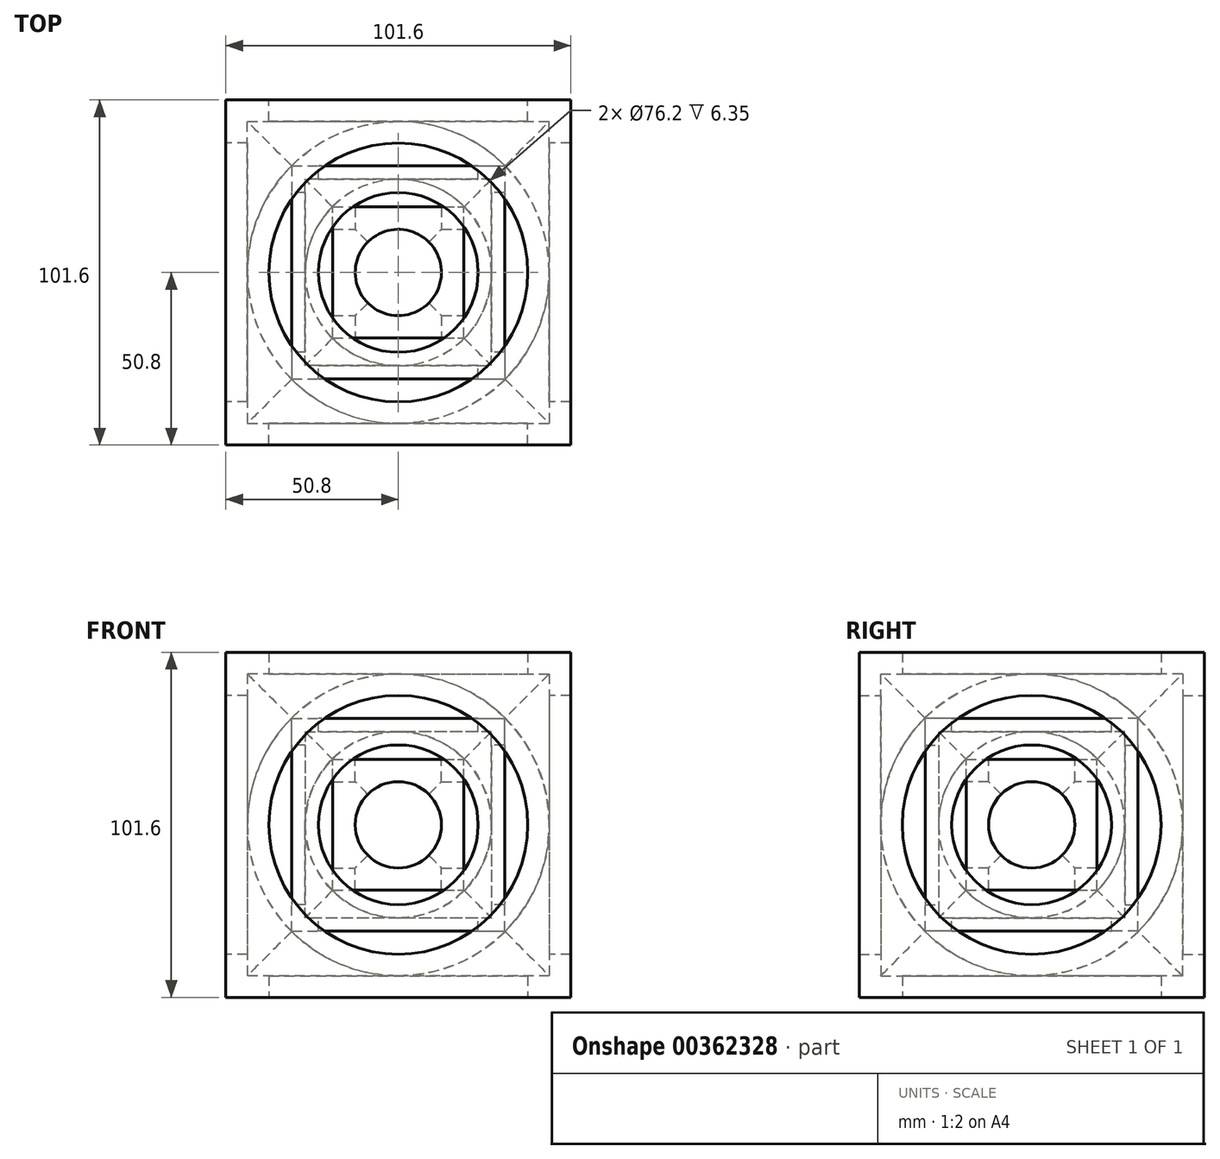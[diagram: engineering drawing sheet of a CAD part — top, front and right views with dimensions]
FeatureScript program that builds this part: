
annotation { "Feature Type Name" : "Feature", "Feature Type Description" : "" }
export const myFeature = defineFeature(function(context is Context, id is Id, definition is map)
    precondition{}
    {
        {
            var Q0;
            Q0=qCreatedBy(makeId("Front.planeOp"),FACE);
            var sketch = newSketch(context, id + "F0", { "sketchPlane" : qUnion([Q0])});
            skLineSegment(sketch, "E0.bottom", {"start": v(-50.8, 50.8) * mm, "end": v(50.8, 50.8) * mm});
            skLineSegment(sketch, "E0.top", {"start": v(-50.8, -50.8) * mm, "end": v(50.8, -50.8) * mm});
            skLineSegment(sketch, "E0.left", {"start": v(-50.8, 50.8) * mm, "end": v(-50.8, -50.8) * mm});
            skLineSegment(sketch, "E0.right", {"start": v(50.8, 50.8) * mm, "end": v(50.8, -50.8) * mm});
            skLineSegment(sketch, "E1", {"start": v(-50.8, 50.8) * mm, "end": v(50.8, -50.8) * mm, "construction": true});
            skSolve(sketch);
        }
        {
            var Q0;
            Q0 = qSketchRegion(id + "F0", true);
            extrude(context, id + "F1", {"entities" : qUnion([Q0]), "endBound" : BoundingType.SYMMETRIC, "depth" : 101.6 * mm});
        }
        {
            var Q0;
            Q0=qCreatedBy(makeId("Top.planeOp"),FACE);
            var sketch = newSketch(context, id + "F2", { "sketchPlane" : qUnion([Q0])});
            skLineSegment(sketch, "E2.bottom", {"start": v(-50.8, 0) * mm, "end": v(-31.34, 0) * mm});
            skLineSegment(sketch, "E2.top", {"start": v(-50.8, 38.1) * mm, "end": v(-44.45, 38.1) * mm});
            skLineSegment(sketch, "E2.left", {"start": v(-50.8, 0) * mm, "end": v(-50.8, 38.1) * mm});
            skLineSegment(sketch, "E3.left", {"start": v(-44.45, 38.1) * mm, "end": v(-44.45, 44.45) * mm});
            skLineSegment(sketch, "E4.bottom", {"start": v(0, 31.34) * mm, "end": v(0, 50.8) * mm});
            skLineSegment(sketch, "E4.top", {"start": v(-38.1, 44.45) * mm, "end": v(-38.1, 50.8) * mm});
            skLineSegment(sketch, "E4.left", {"start": v(0, 50.8) * mm, "end": v(-38.1, 50.8) * mm});
            skLineSegment(sketch, "E5.top", {"start": v(-44.45, 31.34) * mm, "end": v(-44.45, 44.45) * mm});
            skLineSegment(sketch, "E5.right", {"start": v(0, 31.34) * mm, "end": v(-44.45, 31.34) * mm});
            skLineSegment(sketch, "E6", {"start": v(-38.1, 44.45) * mm, "end": v(-44.45, 44.45) * mm});
            skLineSegment(sketch, "E7", {"start": v(-44.45, 44.45) * mm, "end": v(-31.34, 44.45) * mm});
            skLineSegment(sketch, "E8", {"start": v(-31.34, 44.45) * mm, "end": v(-31.34, 0) * mm});
            skLineSegment(sketch, "E9.bottom", {"start": v(-50.8, 50.8) * mm, "end": v(-38.1, 50.8) * mm, "construction": true});
            skLineSegment(sketch, "E9.top", {"start": v(-50.8, 38.1) * mm, "end": v(-38.1, 38.1) * mm, "construction": true});
            skLineSegment(sketch, "E9.left", {"start": v(-50.8, 50.8) * mm, "end": v(-50.8, 38.1) * mm, "construction": true});
            skLineSegment(sketch, "E9.right", {"start": v(-38.1, 50.8) * mm, "end": v(-38.1, 38.1) * mm, "construction": true});
            skLineSegment(sketch, "E10.MirrorCS", {"start": v(0, -31.34) * mm, "end": v(-44.45, -31.34) * mm});
            skLineSegment(sketch, "E11.MirrorCS", {"start": v(-44.45, -31.34) * mm, "end": v(-44.45, -44.45) * mm});
            skLineSegment(sketch, "E12.MirrorCS", {"start": v(0, -31.34) * mm, "end": v(0, -50.8) * mm});
            skLineSegment(sketch, "E13.MirrorCS", {"start": v(0, -50.8) * mm, "end": v(-38.1, -50.8) * mm});
            skLineSegment(sketch, "E14.MirrorCS", {"start": v(-38.1, -44.45) * mm, "end": v(-38.1, -50.8) * mm});
            skLineSegment(sketch, "E15.MirrorCS", {"start": v(-38.1, -44.45) * mm, "end": v(-44.45, -44.45) * mm});
            skLineSegment(sketch, "E16.MirrorCS", {"start": v(31.34, 44.45) * mm, "end": v(31.34, 0) * mm});
            skLineSegment(sketch, "E17.MirrorCS", {"start": v(44.45, 44.45) * mm, "end": v(31.34, 44.45) * mm});
            skLineSegment(sketch, "E18.MirrorCS", {"start": v(50.8, 0) * mm, "end": v(31.34, 0) * mm});
            skLineSegment(sketch, "E19.MirrorCS", {"start": v(50.8, 0) * mm, "end": v(50.8, 38.1) * mm});
            skLineSegment(sketch, "E20.MirrorCS", {"start": v(50.8, 38.1) * mm, "end": v(44.45, 38.1) * mm});
            skLineSegment(sketch, "E21.MirrorCS", {"start": v(44.45, 38.1) * mm, "end": v(44.45, 44.45) * mm});
            skSolve(sketch);
        }
        {
            var Q0;
            Q0=makeQuery(id+"F2.imprint","IMPRINT",FACE,{"disambiguationData":[TD([[makeQuery(id+"F2.imprint","IMPRINT",EDGE,{"derivedFrom":sQuery(id+"F2.wireOp",EDGE,"E2.bottom")}),1.0]])]});
            var Q1;
            {var subQ0=sQuery(id+"F2.wireOp",EDGE,"E5.top");Q1=makeQuery(id+"F2.imprint","IMPRINT",FACE,{"disambiguationData":[TD([[makeQuery(id+"F2.imprint","IMPRINT",EDGE,{"derivedFrom":subQ0}),-1.0]])]});}
            var Q2;
            Q2=makeQuery(id+"F2.imprint","IMPRINT",FACE,{"disambiguationData":[TD([[makeQuery(id+"F2.imprint","IMPRINT",EDGE,{"derivedFrom":sQuery(id+"F2.wireOp",EDGE,"E16.MirrorCS")}),1.0]])]});
            var Q3;
            Q3=sQuery(id+"F2.wireOp",EDGE,"E2.bottom");
            revolve(context, id + "F3", {"operationType" : NewBodyOperationType.REMOVE, "entities" : qUnion([Q0, Q1, Q2]), "axis" : qUnion([Q3]), "revolveType" : RevolveType.FULL});
        }
        {
            var Q0;
            Q0=makeQuery(id+"F2.imprint","IMPRINT",FACE,{"disambiguationData":[TD([[makeQuery(id+"F2.imprint","IMPRINT",EDGE,{"derivedFrom":sQuery(id+"F2.wireOp",EDGE,"E4.bottom")}),1.0]])]});
            var Q1;
            {var subQ0=sQuery(id+"F2.wireOp",EDGE,"E5.top");Q1=makeQuery(id+"F2.imprint","IMPRINT",FACE,{"disambiguationData":[TD([[makeQuery(id+"F2.imprint","IMPRINT",EDGE,{"derivedFrom":subQ0}),-1.0]])]});}
            var Q2;
            Q2=makeQuery(id+"F2.imprint","IMPRINT",FACE,{"disambiguationData":[TD([[makeQuery(id+"F2.imprint","IMPRINT",EDGE,{"derivedFrom":sQuery(id+"F2.wireOp",EDGE,"E10.MirrorCS")}),1.0]])]});
            var Q3;
            Q3=sQuery(id+"F2.wireOp",EDGE,"E4.bottom");
            revolve(context, id + "F4", {"operationType" : NewBodyOperationType.REMOVE, "entities" : qUnion([Q0, Q1, Q2]), "axis" : qUnion([Q3]), "revolveType" : RevolveType.FULL, "oppositeDirection" : true});
        }
        {
            var Q0;
            Q0=qCreatedBy(makeId("Front.planeOp"),FACE);
            var sketch = newSketch(context, id + "F5", { "sketchPlane" : qUnion([Q0])});
            skLineSegment(sketch, "E22.bottom", {"start": v(0, 50.8) * mm, "end": v(-38.1, 50.8) * mm});
            skLineSegment(sketch, "E22.right", {"start": v(-38.1, 50.8) * mm, "end": v(-38.1, 44.45) * mm});
            skLineSegment(sketch, "E23.bottom", {"start": v(-44.45, 31.34) * mm, "end": v(0, 31.34) * mm});
            skLineSegment(sketch, "E23.top", {"start": v(-44.45, 44.45) * mm, "end": v(-38.1, 44.45) * mm});
            skLineSegment(sketch, "E23.left", {"start": v(-44.45, 31.34) * mm, "end": v(-44.45, 44.45) * mm});
            skLineSegment(sketch, "E24", {"start": v(0, 50.8) * mm, "end": v(0, 31.34) * mm});
            skLineSegment(sketch, "E25.MirrorCS", {"start": v(0, -50.8) * mm, "end": v(-38.1, -50.8) * mm});
            skLineSegment(sketch, "E26.MirrorCS", {"start": v(0, -50.8) * mm, "end": v(0, -31.34) * mm});
            skLineSegment(sketch, "E27.MirrorCS", {"start": v(-44.45, -31.34) * mm, "end": v(0, -31.34) * mm});
            skLineSegment(sketch, "E28.MirrorCS", {"start": v(-44.45, -31.34) * mm, "end": v(-44.45, -44.45) * mm});
            skLineSegment(sketch, "E29.MirrorCS", {"start": v(-38.1, -50.8) * mm, "end": v(-38.1, -44.45) * mm});
            skLineSegment(sketch, "E30.MirrorCS", {"start": v(-44.45, -44.45) * mm, "end": v(-38.1, -44.45) * mm});
            skLineSegment(sketch, "E31", {"start": v(-50.8, 0) * mm, "end": v(-50.8, 38.1) * mm, "construction": true});
            skLineSegment(sketch, "E32", {"start": v(-50.8, 38.1) * mm, "end": v(-44.45, 38.1) * mm, "construction": true});
            skLineSegment(sketch, "E33", {"start": v(-44.45, 38.1) * mm, "end": v(-44.45, 44.45) * mm, "construction": true});
            skLineSegment(sketch, "E34", {"start": v(-44.45, 44.45) * mm, "end": v(-31.34, 44.45) * mm, "construction": true});
            skLineSegment(sketch, "E35", {"start": v(-31.34, 44.45) * mm, "end": v(-31.34, 0) * mm, "construction": true});
            skLineSegment(sketch, "E36", {"start": v(-31.34, 0) * mm, "end": v(-50.8, 0) * mm, "construction": true});
            skLineSegment(sketch, "E37.bottom", {"start": v(-38.1, 50.8) * mm, "end": v(-50.8, 50.8) * mm, "construction": true});
            skLineSegment(sketch, "E37.top", {"start": v(-38.1, 38.1) * mm, "end": v(-50.8, 38.1) * mm, "construction": true});
            skLineSegment(sketch, "E37.left", {"start": v(-38.1, 50.8) * mm, "end": v(-38.1, 38.1) * mm, "construction": true});
            skLineSegment(sketch, "E37.right", {"start": v(-50.8, 50.8) * mm, "end": v(-50.8, 38.1) * mm, "construction": true});
            skSolve(sketch);
        }
        {
            var Q0;
            Q0 = qSketchRegion(id + "F5", true);
            var Q1;
            Q1=sQuery(id+"F5.wireOp",EDGE,"E24");
            revolve(context, id + "F6", {"operationType" : NewBodyOperationType.REMOVE, "entities" : qUnion([Q0]), "axis" : qUnion([Q1]), "revolveType" : RevolveType.FULL, "oppositeDirection" : true});
        }
        {
            var Q0;
            Q0=qCreatedBy(makeId("Top.planeOp"),FACE);
            var sketch = newSketch(context, id + "F7", { "sketchPlane" : qUnion([Q0])});
            skLineSegment(sketch, "E38", {"start": v(-31.34, 0) * mm, "end": v(-31.34, 23.5) * mm});
            skLineSegment(sketch, "E39", {"start": v(-31.34, 23.5) * mm, "end": v(-27.43, 23.5) * mm});
            skLineSegment(sketch, "E40", {"start": v(-27.43, 23.5) * mm, "end": v(-27.43, 27.43) * mm});
            skLineSegment(sketch, "E41", {"start": v(-27.43, 27.43) * mm, "end": v(-19.28, 27.43) * mm});
            skLineSegment(sketch, "E42", {"start": v(-19.28, 27.43) * mm, "end": v(-19.28, 0) * mm});
            skLineSegment(sketch, "E43", {"start": v(-19.28, 0) * mm, "end": v(-31.34, 0) * mm});
            skLineSegment(sketch, "E44", {"start": v(0, 31.34) * mm, "end": v(-23.5, 31.34) * mm});
            skLineSegment(sketch, "E45", {"start": v(-23.5, 31.34) * mm, "end": v(-23.5, 27.43) * mm});
            skLineSegment(sketch, "E46", {"start": v(-23.5, 27.43) * mm, "end": v(-27.43, 27.43) * mm});
            skLineSegment(sketch, "E47", {"start": v(-27.43, 27.43) * mm, "end": v(-27.43, 19.28) * mm});
            skLineSegment(sketch, "E48", {"start": v(-27.43, 19.28) * mm, "end": v(0, 19.28) * mm});
            skLineSegment(sketch, "E49", {"start": v(0, 19.28) * mm, "end": v(0, 31.34) * mm});
            skLineSegment(sketch, "E50.bottom", {"start": v(-31.34, 31.34) * mm, "end": v(-23.5, 31.34) * mm, "construction": true});
            skLineSegment(sketch, "E50.top", {"start": v(-31.34, 23.5) * mm, "end": v(-23.5, 23.5) * mm, "construction": true});
            skLineSegment(sketch, "E50.left", {"start": v(-31.34, 31.34) * mm, "end": v(-31.34, 23.5) * mm, "construction": true});
            skLineSegment(sketch, "E50.right", {"start": v(-23.5, 31.34) * mm, "end": v(-23.5, 23.5) * mm, "construction": true});
            skLineSegment(sketch, "E51.MirrorCS", {"start": v(19.28, 27.43) * mm, "end": v(19.28, 0) * mm});
            skLineSegment(sketch, "E52.MirrorCS", {"start": v(31.34, 0) * mm, "end": v(31.34, 23.5) * mm});
            skLineSegment(sketch, "E53.MirrorCS", {"start": v(31.34, 23.5) * mm, "end": v(27.43, 23.5) * mm});
            skLineSegment(sketch, "E54.MirrorCS", {"start": v(27.43, 23.5) * mm, "end": v(27.43, 27.43) * mm});
            skLineSegment(sketch, "E55.MirrorCS", {"start": v(27.43, 27.43) * mm, "end": v(19.28, 27.43) * mm});
            skLineSegment(sketch, "E56.MirrorCS", {"start": v(19.28, 0) * mm, "end": v(31.34, 0) * mm});
            skLineSegment(sketch, "E57.MirrorCS", {"start": v(-27.43, -19.28) * mm, "end": v(0, -19.28) * mm});
            skLineSegment(sketch, "E58.MirrorCS", {"start": v(0, -31.34) * mm, "end": v(-23.5, -31.34) * mm});
            skLineSegment(sketch, "E59.MirrorCS", {"start": v(0, -19.28) * mm, "end": v(0, -31.34) * mm});
            skLineSegment(sketch, "E60.MirrorCS", {"start": v(-27.43, -27.43) * mm, "end": v(-27.43, -19.28) * mm});
            skLineSegment(sketch, "E61.MirrorCS", {"start": v(-23.5, -27.43) * mm, "end": v(-27.43, -27.43) * mm});
            skLineSegment(sketch, "E62.MirrorCS", {"start": v(-23.5, -31.34) * mm, "end": v(-23.5, -27.43) * mm});
            skSolve(sketch);
        }
        {
            var Q0;
            {var subQ1=sQuery(id+"F7.wireOp",EDGE,"E41");Q0=makeQuery(id+"F7.imprint","IMPRINT",FACE,{"disambiguationData":[TD([[makeQuery(id+"F7.imprint","IMPRINT",EDGE,{"derivedFrom":subQ1}),1.0]])]});}
            var Q1;
            {var subQ4=sQuery(id+"F7.wireOp",EDGE,"E41");Q1=makeQuery(id+"F7.imprint","IMPRINT",FACE,{"disambiguationData":[TD([[makeQuery(id+"F7.imprint","IMPRINT",EDGE,{"derivedFrom":subQ4}),-1.0]])]});}
            var Q2;
            Q2=makeQuery(id+"F7.imprint","IMPRINT",FACE,{"disambiguationData":[TD([[makeQuery(id+"F7.imprint","IMPRINT",EDGE,{"derivedFrom":sQuery(id+"F7.wireOp",EDGE,"E57.MirrorCS")}),-1.0]])]});
            var Q3;
            Q3=sQuery(id+"F7.wireOp",EDGE,"E49");
            revolve(context, id + "F8", {"operationType" : NewBodyOperationType.REMOVE, "entities" : qUnion([Q0, Q1, Q2]), "axis" : qUnion([Q3]), "revolveType" : RevolveType.FULL, "oppositeDirection" : true});
        }
        {
            var Q0;
            Q0=makeQuery(id+"F7.imprint","IMPRINT",FACE,{"disambiguationData":[TD([[makeQuery(id+"F7.imprint","IMPRINT",EDGE,{"derivedFrom":sQuery(id+"F7.wireOp",EDGE,"E38")}),-1.0]])]});
            var Q1;
            {var subQ4=sQuery(id+"F7.wireOp",EDGE,"E41");Q1=makeQuery(id+"F7.imprint","IMPRINT",FACE,{"disambiguationData":[TD([[makeQuery(id+"F7.imprint","IMPRINT",EDGE,{"derivedFrom":subQ4}),-1.0]])]});}
            var Q2;
            Q2=makeQuery(id+"F7.imprint","IMPRINT",FACE,{"disambiguationData":[TD([[makeQuery(id+"F7.imprint","IMPRINT",EDGE,{"derivedFrom":sQuery(id+"F7.wireOp",EDGE,"E51.MirrorCS")}),1.0]])]});
            var Q3;
            Q3=sQuery(id+"F7.wireOp",EDGE,"E43");
            revolve(context, id + "F9", {"operationType" : NewBodyOperationType.REMOVE, "entities" : qUnion([Q0, Q1, Q2]), "axis" : qUnion([Q3]), "revolveType" : RevolveType.FULL, "oppositeDirection" : true});
        }
        {
            var Q0;
            Q0=qCreatedBy(makeId("Front.planeOp"),FACE);
            var sketch = newSketch(context, id + "F10", { "sketchPlane" : qUnion([Q0])});
            skLineSegment(sketch, "E63", {"start": v(-31.34, 0) * mm, "end": v(-31.34, 23.5) * mm, "construction": true});
            skLineSegment(sketch, "E64", {"start": v(-31.34, 23.5) * mm, "end": v(-27.43, 23.5) * mm, "construction": true});
            skLineSegment(sketch, "E65", {"start": v(-27.43, 23.5) * mm, "end": v(-27.43, 27.43) * mm, "construction": true});
            skLineSegment(sketch, "E66", {"start": v(-27.43, 27.43) * mm, "end": v(-19.28, 27.43) * mm, "construction": true});
            skLineSegment(sketch, "E67", {"start": v(-19.28, 27.43) * mm, "end": v(-19.28, 0) * mm, "construction": true});
            skLineSegment(sketch, "E68", {"start": v(-19.28, 0) * mm, "end": v(-31.34, 0) * mm, "construction": true});
            skLineSegment(sketch, "E69", {"start": v(0, 31.34) * mm, "end": v(-23.5, 31.34) * mm});
            skLineSegment(sketch, "E70", {"start": v(-23.5, 31.34) * mm, "end": v(-23.5, 27.43) * mm});
            skLineSegment(sketch, "E71", {"start": v(-23.5, 27.43) * mm, "end": v(-27.43, 27.43) * mm});
            skLineSegment(sketch, "E72", {"start": v(-27.43, 27.43) * mm, "end": v(-27.43, 19.28) * mm});
            skLineSegment(sketch, "E73", {"start": v(-27.43, 19.28) * mm, "end": v(0, 19.28) * mm});
            skLineSegment(sketch, "E74", {"start": v(0, 19.28) * mm, "end": v(0, 31.34) * mm});
            skLineSegment(sketch, "E75.bottom", {"start": v(-31.34, 31.34) * mm, "end": v(-23.5, 31.34) * mm, "construction": true});
            skLineSegment(sketch, "E75.top", {"start": v(-31.34, 23.5) * mm, "end": v(-23.5, 23.5) * mm, "construction": true});
            skLineSegment(sketch, "E75.left", {"start": v(-31.34, 31.34) * mm, "end": v(-31.34, 23.5) * mm, "construction": true});
            skLineSegment(sketch, "E75.right", {"start": v(-23.5, 31.34) * mm, "end": v(-23.5, 23.5) * mm, "construction": true});
            skLineSegment(sketch, "E76.MirrorCS", {"start": v(-27.43, -19.28) * mm, "end": v(0, -19.28) * mm});
            skLineSegment(sketch, "E77.MirrorCS", {"start": v(0, -19.28) * mm, "end": v(0, -31.34) * mm});
            skLineSegment(sketch, "E78.MirrorCS", {"start": v(0, -31.34) * mm, "end": v(-23.5, -31.34) * mm});
            skLineSegment(sketch, "E79.MirrorCS", {"start": v(-27.43, -27.43) * mm, "end": v(-27.43, -19.28) * mm});
            skLineSegment(sketch, "E80.MirrorCS", {"start": v(-23.5, -27.43) * mm, "end": v(-27.43, -27.43) * mm});
            skLineSegment(sketch, "E81.MirrorCS", {"start": v(-23.5, -31.34) * mm, "end": v(-23.5, -27.43) * mm});
            skSolve(sketch);
        }
        {
            var Q0;
            Q0 = qSketchRegion(id + "F10", true);
            var Q1;
            Q1=sQuery(id+"F10.wireOp",EDGE,"E74");
            revolve(context, id + "F11", {"operationType" : NewBodyOperationType.REMOVE, "entities" : qUnion([Q0]), "axis" : qUnion([Q1]), "revolveType" : RevolveType.FULL, "oppositeDirection" : true});
        }
        {
            var Q0;
            Q0=qCreatedBy(makeId("Top.planeOp"),FACE);
            var sketch = newSketch(context, id + "F12", { "sketchPlane" : qUnion([Q0])});
            skCircle(sketch, "E82", {"center": v(0, 0) * mm, "radius": 12.7 * mm});
            skSolve(sketch);
        }
        {
            var Q0;
            Q0 = qSketchRegion(id + "F12", true);
            extrude(context, id + "F13", {"entities" : qUnion([Q0]), "operationType" : NewBodyOperationType.REMOVE, "endBound" : BoundingType.SYMMETRIC, "oppositeDirection" : true, "depth" : 44.45 * mm});
        }
        {
            var Q0;
            Q0=qCreatedBy(makeId("Front.planeOp"),FACE);
            var sketch = newSketch(context, id + "F14", { "sketchPlane" : qUnion([Q0])});
            skCircle(sketch, "E83", {"center": v(0, 0) * mm, "radius": 12.7 * mm});
            skSolve(sketch);
        }
        {
            var Q0;
            Q0 = qSketchRegion(id + "F14", true);
            extrude(context, id + "F15", {"entities" : qUnion([Q0]), "operationType" : NewBodyOperationType.REMOVE, "endBound" : BoundingType.SYMMETRIC, "oppositeDirection" : true, "depth" : 44.45 * mm});
        }
        {
            var Q0;
            Q0=qCreatedBy(makeId("Right.planeOp"),FACE);
            var sketch = newSketch(context, id + "F16", { "sketchPlane" : qUnion([Q0])});
            skCircle(sketch, "E84", {"center": v(0, 0) * mm, "radius": 12.7 * mm});
            skSolve(sketch);
        }
        {
            var Q0;
            Q0 = qSketchRegion(id + "F16", true);
            extrude(context, id + "F17", {"entities" : qUnion([Q0]), "operationType" : NewBodyOperationType.REMOVE, "endBound" : BoundingType.SYMMETRIC, "oppositeDirection" : true, "depth" : 44.45 * mm});
        }
    });
